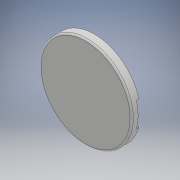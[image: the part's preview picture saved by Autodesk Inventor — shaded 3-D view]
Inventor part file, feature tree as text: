
AUTODESK INVENTOR PART (.ipt)
format: ipt  version: 2018 (Build 220112000, 112)  size: 223,232 bytes
history: native  units: mm
features: extrude x5, sketch x5, fillet x2, pattern_circular x1
ambient origin geometry x8: Origin, YZ Plane, XZ Plane, XY Plane, X Axis, Y Axis, Z Axis, Center Point
bodies: Solid1 (feature_tree)
feature tree (13):
  extrude  "Extrusion1"  Depth=0.4mm
  extrude  "Extrusion2"  Depth=5.0mm
  extrude  "Extrusion3"  Depth=27.25mm
  fillet  "Fillet1"  Radius=22.514747mm
  pattern_circular  "Circular Pattern1"  [2 undecoded]
  extrude  "Extrusion4"  Depth=0.5mm
  extrude  "Extrusion7"  Depth=1.4mm TaperAngle=0.0deg
  fillet  "Fillet5"  Radius=0.5mm
  sketch  "Sketch1"  dims[d2=0.4mm d3=0.0mm d4=54.5mm]
  sketch  "Sketch2"  dims[d5=5.0mm d6=0.0mm d7=56.0mm]
  sketch  "Sketch3"  dims[d8=56.0mm d9=27.25mm d10=22.514747mm]
  sketch  "Sketch4"  dims[d11=0.698132mm]
  sketch  "Sketch7"  dims[d12=26.25mm d13=22.514747mm d14=0.698132mm d15=1.4mm d16=0.0mm d17=0.5mm d18=20.0mm d19=360.0deg d25=7.5mm d26=3.0mm d27=7.5mm d28=3.0mm d29=1.5mm d30=0.0mm d47=48.0mm d48=1.5mm d49=0.0mm d50=54.5mm d51=3.0mm d52=7.5mm d53=3.0mm d54=7.5mm d55=1.0mm d56=0.5mm]
note: 2 required parameter values undecoded (feature->parameter linkage not recoverable at this tier; creation-order binding heuristic only, values carry confidence <= 0.55)
